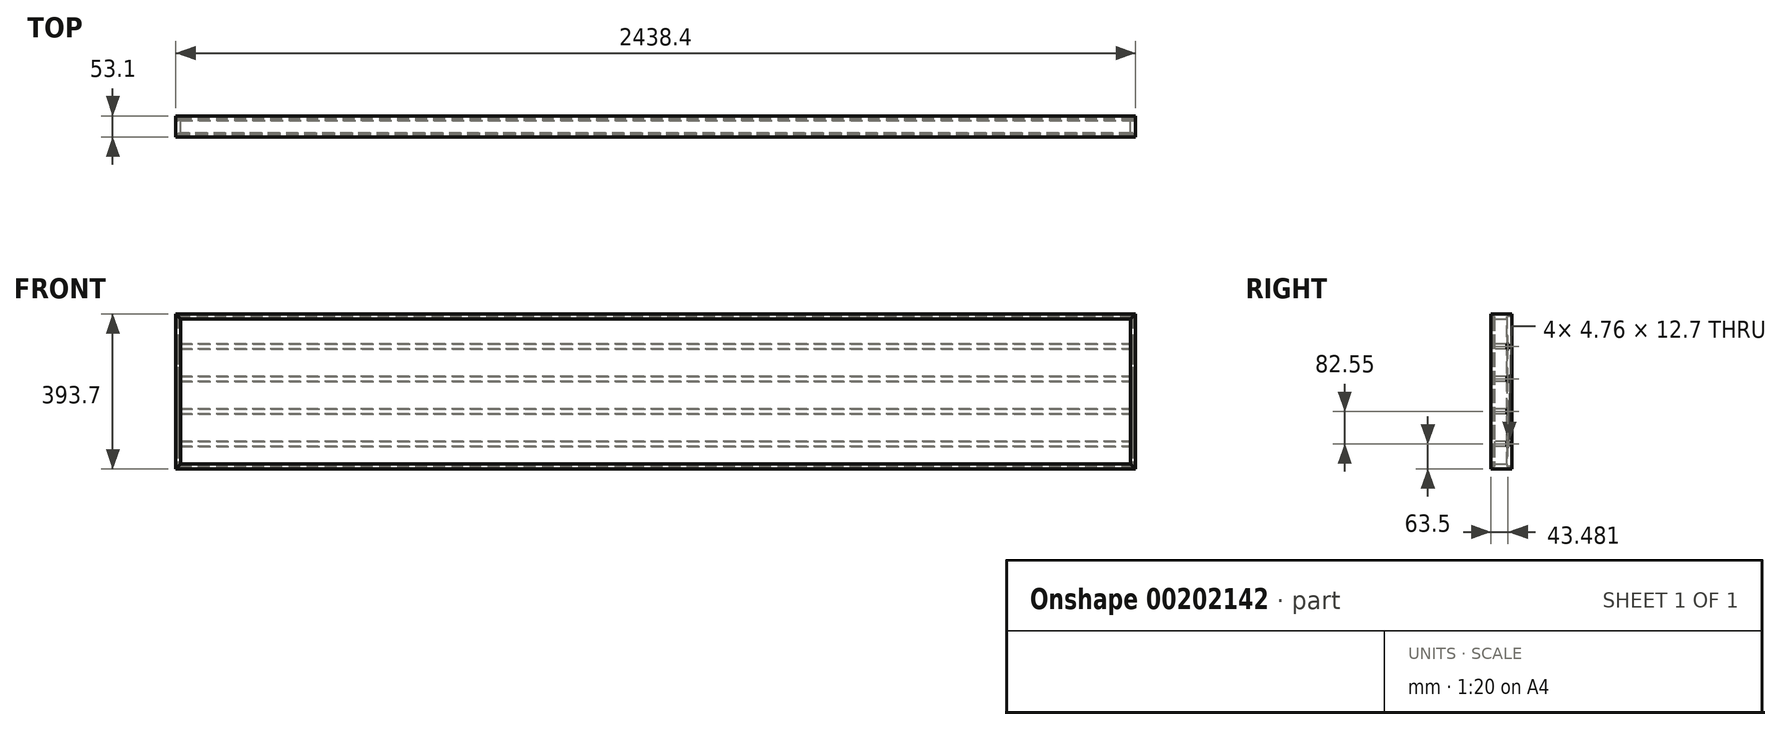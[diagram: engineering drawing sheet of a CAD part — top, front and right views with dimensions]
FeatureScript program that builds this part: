
annotation { "Feature Type Name" : "Feature", "Feature Type Description" : "" }
export const myFeature = defineFeature(function(context is Context, id is Id, definition is map)
    precondition{}
    {
        {
            var Q0;
            Q0=qCreatedBy(makeId("Right.planeOp"),FACE);
            var sketch = newSketch(context, id + "F0", { "sketchPlane" : qUnion([Q0])});
            skLineSegment(sketch, "E0.bottom", {"start": v(0, 0) * mm, "end": v(-12, 0) * mm});
            skLineSegment(sketch, "E0.top", {"start": v(0, -393.7) * mm, "end": v(-12, -393.7) * mm});
            skLineSegment(sketch, "E0.left", {"start": v(0, 0) * mm, "end": v(0, -393.7) * mm});
            skLineSegment(sketch, "E0.right", {"start": v(-12, 0) * mm, "end": v(-12, -393.7) * mm});
            skLineSegment(sketch, "E1.bottom", {"start": v(0, 0) * mm, "end": v(-53.1, 0) * mm});
            skLineSegment(sketch, "E1.top", {"start": v(0, -12.7) * mm, "end": v(-53.1, -12.7) * mm});
            skLineSegment(sketch, "E1.left", {"start": v(0, 0) * mm, "end": v(0, -12.7) * mm});
            skLineSegment(sketch, "E1.right", {"start": v(-53.1, 0) * mm, "end": v(-53.1, -12.7) * mm});
            skLineSegment(sketch, "E2.bottom", {"start": v(-7.24, -76.2) * mm, "end": v(-43.75, -76.2) * mm});
            skLineSegment(sketch, "E2.top", {"start": v(-7.24, -88.9) * mm, "end": v(-43.75, -88.9) * mm});
            skLineSegment(sketch, "E2.left", {"start": v(-7.24, -76.2) * mm, "end": v(-7.24, -88.9) * mm});
            skLineSegment(sketch, "E2.right", {"start": v(-43.75, -76.2) * mm, "end": v(-43.75, -88.9) * mm});
            skLineSegment(sketch, "E3.0.1.0", {"start": v(-7.24, -152.4) * mm, "end": v(-7.24, -165.1) * mm});
            skLineSegment(sketch, "E3.0.1.1", {"start": v(-7.24, -152.4) * mm, "end": v(-43.75, -152.4) * mm});
            skLineSegment(sketch, "E3.0.1.2", {"start": v(-43.75, -152.4) * mm, "end": v(-43.75, -165.1) * mm});
            skLineSegment(sketch, "E3.0.1.3", {"start": v(-7.24, -165.1) * mm, "end": v(-43.75, -165.1) * mm});
            skLineSegment(sketch, "E3.0.2.0", {"start": v(-7.24, -228.6) * mm, "end": v(-7.24, -241.3) * mm});
            skLineSegment(sketch, "E3.0.2.1", {"start": v(-7.24, -228.6) * mm, "end": v(-43.75, -228.6) * mm});
            skLineSegment(sketch, "E3.0.2.2", {"start": v(-43.75, -228.6) * mm, "end": v(-43.75, -241.3) * mm});
            skLineSegment(sketch, "E3.0.2.3", {"start": v(-7.24, -241.3) * mm, "end": v(-43.75, -241.3) * mm});
            skLineSegment(sketch, "E3.0.3.0", {"start": v(-7.24, -304.8) * mm, "end": v(-7.24, -317.5) * mm});
            skLineSegment(sketch, "E3.0.3.1", {"start": v(-7.24, -304.8) * mm, "end": v(-43.75, -304.8) * mm});
            skLineSegment(sketch, "E3.0.3.2", {"start": v(-43.75, -304.8) * mm, "end": v(-43.75, -317.5) * mm});
            skLineSegment(sketch, "E3.0.3.3", {"start": v(-7.24, -317.5) * mm, "end": v(-43.75, -317.5) * mm});
            skLineSegment(sketch, "E3.direction1", {"start": v(-43.75, -88.9) * mm, "end": v(-15.38, -88.9) * mm, "construction": true});
            skLineSegment(sketch, "E3.direction2", {"start": v(-43.75, -88.9) * mm, "end": v(-43.75, -165.1) * mm, "construction": true});
            skLineSegment(sketch, "E4.bottom", {"start": v(0, -393.7) * mm, "end": v(-53.1, -393.7) * mm});
            skLineSegment(sketch, "E4.top", {"start": v(0, -381) * mm, "end": v(-53.1, -381) * mm});
            skLineSegment(sketch, "E4.left", {"start": v(0, -393.7) * mm, "end": v(0, -381) * mm});
            skLineSegment(sketch, "E4.right", {"start": v(-53.1, -393.7) * mm, "end": v(-53.1, -381) * mm});
            skLineSegment(sketch, "E5", {"start": v(-25.5, -76.2) * mm, "end": v(-25.5, -12.7) * mm, "construction": true});
            skLineSegment(sketch, "E6", {"start": v(-25.5, -88.9) * mm, "end": v(-25.5, -152.4) * mm, "construction": true});
            skLineSegment(sketch, "E7", {"start": v(-25.5, -317.5) * mm, "end": v(-25.5, -381) * mm, "construction": true});
            skLineSegment(sketch, "E8.bottom", {"start": v(-43.75, -6.35) * mm, "end": v(-46.75, -6.35) * mm, "construction": true});
            skLineSegment(sketch, "E8.top", {"start": v(-43.75, -387.35) * mm, "end": v(-46.75, -387.35) * mm, "construction": true});
            skLineSegment(sketch, "E8.left", {"start": v(-43.75, -6.35) * mm, "end": v(-43.75, -387.35) * mm, "construction": true});
            skLineSegment(sketch, "E8.right", {"start": v(-46.75, -6.35) * mm, "end": v(-46.75, -387.35) * mm, "construction": true});
            skSolve(sketch);
        }
        {
            var Q0;
            Q0=qCreatedBy(makeId("Right.planeOp"),FACE);
            var sketch = newSketch(context, id + "F1", { "sketchPlane" : qUnion([Q0])});
            skLineSegment(sketch, "E9.0", {"start": v(-12, 0) * mm, "end": v(-12, -393.7) * mm, "construction": true});
            skLineSegment(sketch, "E10.0", {"start": v(0, 0) * mm, "end": v(-53.1, 0) * mm});
            skLineSegment(sketch, "E10.1", {"start": v(-53.1, 0) * mm, "end": v(-53.1, -12.7) * mm});
            skLineSegment(sketch, "E10.2", {"start": v(0, -12.7) * mm, "end": v(-53.1, -12.7) * mm});
            skLineSegment(sketch, "E10.3", {"start": v(0, 0) * mm, "end": v(0, -12.7) * mm});
            skSolve(sketch);
        }
        {
            var Q0;
            Q0 = qSketchRegion(id + "F1", true);
            extrude(context, id + "F2", {"entities" : qUnion([Q0]), "depth" : 1219.2 * mm, "hasSecondDirection" : true, "secondDirectionOppositeDirection" : true, "secondDirectionDepth" : 1219.2 * mm});
        }
        {
            var Q0;
            Q0=qCreatedBy(makeId("Right.planeOp"),FACE);
            var sketch = newSketch(context, id + "F3", { "sketchPlane" : qUnion([Q0])});
            skLineSegment(sketch, "E11.0", {"start": v(-12, 0) * mm, "end": v(-12, -393.7) * mm, "construction": true});
            skLineSegment(sketch, "E12.0", {"start": v(0, -393.7) * mm, "end": v(-53.1, -393.7) * mm});
            skLineSegment(sketch, "E12.1", {"start": v(-53.1, -393.7) * mm, "end": v(-53.1, -381) * mm});
            skLineSegment(sketch, "E12.2", {"start": v(0, -381) * mm, "end": v(-53.1, -381) * mm});
            skLineSegment(sketch, "E12.3", {"start": v(0, -393.7) * mm, "end": v(0, -381) * mm});
            skSolve(sketch);
        }
        {
            var Q0;
            Q0 = qSketchRegion(id + "F3", true);
            extrude(context, id + "F4", {"entities" : qUnion([Q0]), "depth" : 1219.2 * mm, "hasSecondDirection" : true, "secondDirectionOppositeDirection" : true, "secondDirectionDepth" : 1219.2 * mm});
        }
        {
            var Q0;
            Q0=qCreatedBy(makeId("Right.planeOp"),FACE);
            var sketch = newSketch(context, id + "F5", { "sketchPlane" : qUnion([Q0])});
            skPoint(sketch, "E13.orphan", {"position": v(-43.75, -76.2) * mm});
            skPoint(sketch, "E14.orphan", {"position": v(-43.75, -88.9) * mm});
            skPoint(sketch, "E15.orphan", {"position": v(-43.75, -152.4) * mm});
            skPoint(sketch, "E16.orphan", {"position": v(-43.75, -165.1) * mm});
            skPoint(sketch, "E17.orphan", {"position": v(-43.75, -228.6) * mm});
            skPoint(sketch, "E18.orphan", {"position": v(-43.75, -241.3) * mm});
            skPoint(sketch, "E19.orphan", {"position": v(-43.75, -304.8) * mm});
            skPoint(sketch, "E20.orphan", {"position": v(-43.75, -317.5) * mm});
            skLineSegment(sketch, "E21.bottom", {"start": v(0, -6.35) * mm, "end": v(-12, -6.35) * mm});
            skLineSegment(sketch, "E21.top", {"start": v(0, -387.35) * mm, "end": v(-12, -387.35) * mm});
            skLineSegment(sketch, "E21.left", {"start": v(0, -6.35) * mm, "end": v(0, -387.35) * mm});
            skLineSegment(sketch, "E21.right", {"start": v(-12, -6.35) * mm, "end": v(-12, -387.35) * mm});
            skSolve(sketch);
        }
        {
            var Q0;
            Q0 = qSketchRegion(id + "F5", true);
            extrude(context, id + "F6", {"entities" : qUnion([Q0]), "depth" : 1212.85 * mm, "hasSecondDirection" : true, "secondDirectionOppositeDirection" : true, "secondDirectionDepth" : 1212.85 * mm});
        }
        {
            var Q0;
            Q0=qCreatedBy(makeId("Front.planeOp"),FACE);
            var sketch = newSketch(context, id + "F7", { "sketchPlane" : qUnion([Q0])});
            skPoint(sketch, "E22.0", {"position": v(-1219.2, 0) * mm});
            skLineSegment(sketch, "E23.left", {"start": v(-1219.2, 0) * mm, "end": v(-1219.2, -393.7) * mm});
            skLineSegment(sketch, "E23.right", {"start": v(-1206.5, -12.7) * mm, "end": v(-1206.5, -381) * mm});
            skLineSegment(sketch, "E24", {"start": v(-1219.2, 0) * mm, "end": v(-1206.5, -12.7) * mm});
            skLineSegment(sketch, "E25", {"start": v(-1219.2, -393.7) * mm, "end": v(-1206.5, -381) * mm});
            skPoint(sketch, "E26.0", {"position": v(1219.2, 0) * mm});
            skPoint(sketch, "E26.1", {"position": v(1219.2, -393.7) * mm});
            skLineSegment(sketch, "E27.left", {"start": v(1219.2, 0) * mm, "end": v(1219.2, -393.7) * mm});
            skLineSegment(sketch, "E27.right", {"start": v(1206.5, -12.7) * mm, "end": v(1206.5, -381) * mm});
            skLineSegment(sketch, "E28", {"start": v(1219.2, 0) * mm, "end": v(1206.5, -12.7) * mm});
            skLineSegment(sketch, "E29", {"start": v(1219.2, -393.7) * mm, "end": v(1206.5, -381) * mm});
            skSolve(sketch);
        }
        {
            var Q0;
            Q0 = qSketchRegion(id + "F7", true);
            var Q1;
            Q1=makeQuery(id+"F2.opExtrude","SWEPT_FACE",FACE,{"disambiguationData":[OSD([sQuery(id+"F1.wireOp",EDGE,"E10.1")])]});
            extrude(context, id + "F8", {"entities" : qUnion([Q0]), "endBound" : BoundingType.UP_TO_SURFACE, "endBoundEntityFace" : qUnion([Q1]), "depth" : 63.5 * mm});
        }
        {
            var Q0;
            Q0=qCreatedBy(makeId("Right.planeOp"),FACE);
            var sketch = newSketch(context, id + "F9", { "sketchPlane" : qUnion([Q0])});
            skLineSegment(sketch, "E30.0", {"start": v(-7.24, -76.2) * mm, "end": v(-43.75, -76.2) * mm});
            skLineSegment(sketch, "E30.1", {"start": v(-43.75, -76.2) * mm, "end": v(-43.75, -88.9) * mm});
            skLineSegment(sketch, "E30.2", {"start": v(-7.24, -88.9) * mm, "end": v(-43.75, -88.9) * mm});
            skLineSegment(sketch, "E30.3", {"start": v(-7.24, -76.2) * mm, "end": v(-7.24, -88.9) * mm});
            skSolve(sketch);
        }
        {
            var Q0;
            Q0 = qSketchRegion(id + "F9", true);
            var Q1;
            Q1=makeQuery(id+"F8.opExtrude","SWEPT_FACE",FACE,{"disambiguationData":[OSD([sQuery(id+"F7.wireOp",EDGE,"E27.right")])]});
            var Q2;
            Q2=makeQuery(id+"F8.opExtrude","SWEPT_FACE",FACE,{"disambiguationData":[OSD([sQuery(id+"F7.wireOp",EDGE,"E23.right")])]});
            extrude(context, id + "F10", {"entities" : qUnion([Q0]), "endBound" : BoundingType.UP_TO_SURFACE, "endBoundEntityFace" : qUnion([Q1]), "depth" : 1206.5 * mm, "hasSecondDirection" : true, "secondDirectionBound" : BoundingType.UP_TO_SURFACE, "secondDirectionOppositeDirection" : true, "secondDirectionBoundEntityFace" : qUnion([Q2]), "secondDirectionDepth" : 1206.5 * mm});
        }
        {
            var Q0;
            Q0=makeQuery(id+"F10.opExtrude","SWEPT_BODY",BODY,{"disambiguationData":[OSD([sQuery(id+"F9.wireOp",EDGE,"E30.0"),sQuery(id+"F9.wireOp",EDGE,"E30.1"),sQuery(id+"F9.wireOp",EDGE,"E30.2"),sQuery(id+"F9.wireOp",EDGE,"E30.3")])]});
            transform(context, id + "F11", {"entities" : qUnion([Q0]), "transformType" : TransformType.TRANSLATION_3D, "dx" : 0 * mm, "dy" : 0 * mm, "dz" : -82.55 * mm, "makeCopy" : true});
        }
        {
            var Q0;
            Q0=makeQuery(id+"F11.opPattern","COPY",BODY,{"derivedFrom":makeQuery(id+"F10.opExtrude","SWEPT_BODY",BODY,{"disambiguationData":[OSD([sQuery(id+"F9.wireOp",EDGE,"E30.0"),sQuery(id+"F9.wireOp",EDGE,"E30.1"),sQuery(id+"F9.wireOp",EDGE,"E30.2"),sQuery(id+"F9.wireOp",EDGE,"E30.3")])]}),"instanceName":"1"});
            transform(context, id + "F12", {"entities" : qUnion([Q0]), "transformType" : TransformType.TRANSLATION_3D, "dx" : 0 * mm, "dy" : 0 * mm, "dz" : -82.55 * mm, "makeCopy" : true});
        }
        {
            var Q0;
            Q0=makeQuery(id+"F12.opPattern","COPY",BODY,{"derivedFrom":makeQuery(id+"F11.opPattern","COPY",BODY,{"derivedFrom":makeQuery(id+"F10.opExtrude","SWEPT_BODY",BODY,{"disambiguationData":[OSD([sQuery(id+"F9.wireOp",EDGE,"E30.0"),sQuery(id+"F9.wireOp",EDGE,"E30.1"),sQuery(id+"F9.wireOp",EDGE,"E30.2"),sQuery(id+"F9.wireOp",EDGE,"E30.3")])]}),"instanceName":"1"}),"instanceName":"1"});
            transform(context, id + "F13", {"entities" : qUnion([Q0]), "transformType" : TransformType.TRANSLATION_3D, "dx" : 0 * mm, "dy" : 0 * mm, "dz" : -82.55 * mm, "makeCopy" : true});
        }
        {
            var Q0;
            Q0=makeQuery(id+"F8.opExtrude","SWEPT_BODY",BODY,{"disambiguationData":[OSD([sQuery(id+"F7.wireOp",EDGE,"E23.left"),sQuery(id+"F7.wireOp",EDGE,"E23.right"),sQuery(id+"F7.wireOp",EDGE,"E24"),sQuery(id+"F7.wireOp",EDGE,"E25")])]});
            var Q1;
            Q1=makeQuery(id+"F8.opExtrude","SWEPT_BODY",BODY,{"disambiguationData":[OSD([sQuery(id+"F7.wireOp",EDGE,"E27.left"),sQuery(id+"F7.wireOp",EDGE,"E27.right"),sQuery(id+"F7.wireOp",EDGE,"E28"),sQuery(id+"F7.wireOp",EDGE,"E29")])]});
            var Q2;
            Q2=makeQuery(id+"F2.opExtrude","SWEPT_BODY",BODY,{"disambiguationData":[OSD([sQuery(id+"F1.wireOp",EDGE,"E10.0"),sQuery(id+"F1.wireOp",EDGE,"E10.1"),sQuery(id+"F1.wireOp",EDGE,"E10.2"),sQuery(id+"F1.wireOp",EDGE,"E10.3")])]});
            var Q3;
            Q3=makeQuery(id+"F4.opExtrude","SWEPT_BODY",BODY,{"disambiguationData":[OSD([sQuery(id+"F3.wireOp",EDGE,"E12.0"),sQuery(id+"F3.wireOp",EDGE,"E12.1"),sQuery(id+"F3.wireOp",EDGE,"E12.2"),sQuery(id+"F3.wireOp",EDGE,"E12.3")])]});
            booleanBodies(context, id + "F14", {"operationType" : BooleanOperationType.SUBTRACTION, "tools" : qUnion([Q0, Q1]), "targets" : qUnion([Q2, Q3]), "keepTools" : true});
        }
        {
            var Q0;
            Q0=makeQuery(id+"F6.opExtrude","SWEPT_BODY",BODY,{"disambiguationData":[OSD([sQuery(id+"F5.wireOp",EDGE,"E21.bottom"),sQuery(id+"F5.wireOp",EDGE,"E21.top"),sQuery(id+"F5.wireOp",EDGE,"E21.left"),sQuery(id+"F5.wireOp",EDGE,"E21.right")])]});
            var Q1;
            Q1=makeQuery(id+"F8.opExtrude","SWEPT_BODY",BODY,{"disambiguationData":[OSD([sQuery(id+"F7.wireOp",EDGE,"E23.left"),sQuery(id+"F7.wireOp",EDGE,"E23.right"),sQuery(id+"F7.wireOp",EDGE,"E24"),sQuery(id+"F7.wireOp",EDGE,"E25")])]});
            var Q2;
            Q2=makeQuery(id+"F8.opExtrude","SWEPT_BODY",BODY,{"disambiguationData":[OSD([sQuery(id+"F7.wireOp",EDGE,"E27.left"),sQuery(id+"F7.wireOp",EDGE,"E27.right"),sQuery(id+"F7.wireOp",EDGE,"E28"),sQuery(id+"F7.wireOp",EDGE,"E29")])]});
            var Q3;
            Q3=makeQuery(id+"F2.opExtrude","SWEPT_BODY",BODY,{"disambiguationData":[OSD([sQuery(id+"F1.wireOp",EDGE,"E10.0"),sQuery(id+"F1.wireOp",EDGE,"E10.1"),sQuery(id+"F1.wireOp",EDGE,"E10.2"),sQuery(id+"F1.wireOp",EDGE,"E10.3")])]});
            var Q4;
            Q4=makeQuery(id+"F4.opExtrude","SWEPT_BODY",BODY,{"disambiguationData":[OSD([sQuery(id+"F3.wireOp",EDGE,"E12.0"),sQuery(id+"F3.wireOp",EDGE,"E12.1"),sQuery(id+"F3.wireOp",EDGE,"E12.2"),sQuery(id+"F3.wireOp",EDGE,"E12.3")])]});
            booleanBodies(context, id + "F15", {"operationType" : BooleanOperationType.SUBTRACTION, "tools" : qUnion([Q0]), "targets" : qUnion([Q1, Q2, Q3, Q4]), "keepTools" : true});
        }
        {
            var Q0;
            Q0=makeQuery(id+"F10.opExtrude","SWEPT_BODY",BODY,{"disambiguationData":[OSD([sQuery(id+"F9.wireOp",EDGE,"E30.0"),sQuery(id+"F9.wireOp",EDGE,"E30.1"),sQuery(id+"F9.wireOp",EDGE,"E30.2"),sQuery(id+"F9.wireOp",EDGE,"E30.3")])]});
            var Q1;
            Q1=makeQuery(id+"F11.opPattern","COPY",BODY,{"derivedFrom":makeQuery(id+"F10.opExtrude","SWEPT_BODY",BODY,{"disambiguationData":[OSD([sQuery(id+"F9.wireOp",EDGE,"E30.0"),sQuery(id+"F9.wireOp",EDGE,"E30.1"),sQuery(id+"F9.wireOp",EDGE,"E30.2"),sQuery(id+"F9.wireOp",EDGE,"E30.3")])]}),"instanceName":"1"});
            var Q2;
            Q2=makeQuery(id+"F12.opPattern","COPY",BODY,{"derivedFrom":makeQuery(id+"F11.opPattern","COPY",BODY,{"derivedFrom":makeQuery(id+"F10.opExtrude","SWEPT_BODY",BODY,{"disambiguationData":[OSD([sQuery(id+"F9.wireOp",EDGE,"E30.0"),sQuery(id+"F9.wireOp",EDGE,"E30.1"),sQuery(id+"F9.wireOp",EDGE,"E30.2"),sQuery(id+"F9.wireOp",EDGE,"E30.3")])]}),"instanceName":"1"}),"instanceName":"1"});
            var Q3;
            Q3=makeQuery(id+"F13.opPattern","COPY",BODY,{"derivedFrom":makeQuery(id+"F12.opPattern","COPY",BODY,{"derivedFrom":makeQuery(id+"F11.opPattern","COPY",BODY,{"derivedFrom":makeQuery(id+"F10.opExtrude","SWEPT_BODY",BODY,{"disambiguationData":[OSD([sQuery(id+"F9.wireOp",EDGE,"E30.0"),sQuery(id+"F9.wireOp",EDGE,"E30.1"),sQuery(id+"F9.wireOp",EDGE,"E30.2"),sQuery(id+"F9.wireOp",EDGE,"E30.3")])]}),"instanceName":"1"}),"instanceName":"1"}),"instanceName":"1"});
            var Q4;
            Q4=makeQuery(id+"F6.opExtrude","SWEPT_BODY",BODY,{"disambiguationData":[OSD([sQuery(id+"F5.wireOp",EDGE,"E21.bottom"),sQuery(id+"F5.wireOp",EDGE,"E21.top"),sQuery(id+"F5.wireOp",EDGE,"E21.left"),sQuery(id+"F5.wireOp",EDGE,"E21.right")])]});
            booleanBodies(context, id + "F16", {"operationType" : BooleanOperationType.SUBTRACTION, "tools" : qUnion([Q0, Q1, Q2, Q3]), "targets" : qUnion([Q4]), "keepTools" : true});
        }
        {
            var Q0;
            Q0=qCreatedBy(makeId("Right.planeOp"),FACE);
            var sketch = newSketch(context, id + "F17", { "sketchPlane" : qUnion([Q0])});
            skLineSegment(sketch, "E31.0.0", {"start": v(-12, -158.75) * mm, "end": v(-12, -171.45) * mm});
            skLineSegment(sketch, "E31.0.1", {"start": v(-12, -171.45) * mm, "end": v(-7.24, -171.45) * mm});
            skLineSegment(sketch, "E31.0.2", {"start": v(-7.24, -171.45) * mm, "end": v(-7.24, -158.75) * mm});
            skLineSegment(sketch, "E31.0.3", {"start": v(-7.24, -158.75) * mm, "end": v(-12, -158.75) * mm});
            skLineSegment(sketch, "E31.1.0", {"start": v(-12, -76.2) * mm, "end": v(-12, -88.9) * mm});
            skLineSegment(sketch, "E31.1.1", {"start": v(-12, -88.9) * mm, "end": v(-7.24, -88.9) * mm});
            skLineSegment(sketch, "E31.1.2", {"start": v(-7.24, -88.9) * mm, "end": v(-7.24, -76.2) * mm});
            skLineSegment(sketch, "E31.1.3", {"start": v(-7.24, -76.2) * mm, "end": v(-12, -76.2) * mm});
            skLineSegment(sketch, "E31.2.0", {"start": v(-12, -241.3) * mm, "end": v(-12, -254) * mm});
            skLineSegment(sketch, "E31.2.1", {"start": v(-12, -254) * mm, "end": v(-7.24, -254) * mm});
            skLineSegment(sketch, "E31.2.2", {"start": v(-7.24, -254) * mm, "end": v(-7.24, -241.3) * mm});
            skLineSegment(sketch, "E31.2.3", {"start": v(-7.24, -241.3) * mm, "end": v(-12, -241.3) * mm});
            skLineSegment(sketch, "E31.3.0", {"start": v(-12, -323.85) * mm, "end": v(-12, -336.55) * mm});
            skLineSegment(sketch, "E31.3.1", {"start": v(-12, -336.55) * mm, "end": v(-7.24, -336.55) * mm});
            skLineSegment(sketch, "E31.3.2", {"start": v(-7.24, -336.55) * mm, "end": v(-7.24, -323.85) * mm});
            skLineSegment(sketch, "E31.3.3", {"start": v(-7.24, -323.85) * mm, "end": v(-12, -323.85) * mm});
            skSolve(sketch);
        }
        {
            var Q0;
            Q0 = qSketchRegion(id + "F17", true);
            extrude(context, id + "F18", {"entities" : qUnion([Q0]), "operationType" : NewBodyOperationType.REMOVE, "endBound" : BoundingType.THROUGH_ALL, "oppositeDirection" : true, "depth" : 25.4 * mm, "hasSecondDirection" : true, "secondDirectionBound" : BoundingType.THROUGH_ALL, "secondDirectionOppositeDirection" : false, "secondDirectionDepth" : 25.4 * mm});
        }
        {
            var Q0;
            Q0=makeQuery(id+"F10.opExtrude","SWEPT_FACE",FACE,{"disambiguationData":[OSD([sQuery(id+"F9.wireOp",EDGE,"E30.1")])]});
            var sketch = newSketch(context, id + "F19", { "sketchPlane" : qUnion([Q0])});
            skLineSegment(sketch, "E32.bottom", {"start": v(-1212.85, -6.35) * mm, "end": v(1212.85, -6.35) * mm});
            skLineSegment(sketch, "E32.top", {"start": v(-1212.85, -387.35) * mm, "end": v(1212.85, -387.35) * mm});
            skLineSegment(sketch, "E32.left", {"start": v(-1212.85, -6.35) * mm, "end": v(-1212.85, -387.35) * mm});
            skLineSegment(sketch, "E32.right", {"start": v(1212.85, -6.35) * mm, "end": v(1212.85, -387.35) * mm});
            skSolve(sketch);
        }
        {
            var Q0;
            Q0 = qSketchRegion(id + "F19", true);
            extrude(context, id + "F20", {"entities" : qUnion([Q0]), "depth" : 3.17 * mm});
        }
        {
            var Q0;
            Q0=makeQuery(id+"F20.opExtrude","SWEPT_BODY",BODY,{"disambiguationData":[OSD([sQuery(id+"F19.wireOp",EDGE,"E32.bottom"),sQuery(id+"F19.wireOp",EDGE,"E32.top"),sQuery(id+"F19.wireOp",EDGE,"E32.left"),sQuery(id+"F19.wireOp",EDGE,"E32.right")])]});
            transform(context, id + "F21", {"entities" : qUnion([Q0]), "transformType" : TransformType.TRANSLATION_3D, "dx" : 0 * mm, "dy" : -1.59 * mm, "dz" : 0 * mm, "makeCopy" : true});
        }
        {
            var Q0;
            Q0=makeQuery(id+"F20.opExtrude","SWEPT_BODY",BODY,{"disambiguationData":[OSD([sQuery(id+"F19.wireOp",EDGE,"E32.bottom"),sQuery(id+"F19.wireOp",EDGE,"E32.top"),sQuery(id+"F19.wireOp",EDGE,"E32.left"),sQuery(id+"F19.wireOp",EDGE,"E32.right")])]});
            var Q1;
            Q1=makeQuery(id+"F8.opExtrude","SWEPT_BODY",BODY,{"disambiguationData":[OSD([sQuery(id+"F7.wireOp",EDGE,"E23.left"),sQuery(id+"F7.wireOp",EDGE,"E23.right"),sQuery(id+"F7.wireOp",EDGE,"E24"),sQuery(id+"F7.wireOp",EDGE,"E25")])]});
            var Q2;
            Q2=makeQuery(id+"F8.opExtrude","SWEPT_BODY",BODY,{"disambiguationData":[OSD([sQuery(id+"F7.wireOp",EDGE,"E27.left"),sQuery(id+"F7.wireOp",EDGE,"E27.right"),sQuery(id+"F7.wireOp",EDGE,"E28"),sQuery(id+"F7.wireOp",EDGE,"E29")])]});
            var Q3;
            Q3=makeQuery(id+"F2.opExtrude","SWEPT_BODY",BODY,{"disambiguationData":[OSD([sQuery(id+"F1.wireOp",EDGE,"E10.0"),sQuery(id+"F1.wireOp",EDGE,"E10.1"),sQuery(id+"F1.wireOp",EDGE,"E10.2"),sQuery(id+"F1.wireOp",EDGE,"E10.3")])]});
            var Q4;
            Q4=makeQuery(id+"F4.opExtrude","SWEPT_BODY",BODY,{"disambiguationData":[OSD([sQuery(id+"F3.wireOp",EDGE,"E12.0"),sQuery(id+"F3.wireOp",EDGE,"E12.1"),sQuery(id+"F3.wireOp",EDGE,"E12.2"),sQuery(id+"F3.wireOp",EDGE,"E12.3")])]});
            booleanBodies(context, id + "F22", {"operationType" : BooleanOperationType.SUBTRACTION, "tools" : qUnion([Q0]), "targets" : qUnion([Q1, Q2, Q3, Q4]), "keepTools" : true});
        }
        {
            var Q0;
            Q0=makeQuery(id+"F21.opPattern","COPY",BODY,{"derivedFrom":makeQuery(id+"F20.opExtrude","SWEPT_BODY",BODY,{"disambiguationData":[OSD([sQuery(id+"F19.wireOp",EDGE,"E32.bottom"),sQuery(id+"F19.wireOp",EDGE,"E32.top"),sQuery(id+"F19.wireOp",EDGE,"E32.left"),sQuery(id+"F19.wireOp",EDGE,"E32.right")])]}),"instanceName":"1"});
            var Q1;
            Q1=makeQuery(id+"F8.opExtrude","SWEPT_BODY",BODY,{"disambiguationData":[OSD([sQuery(id+"F7.wireOp",EDGE,"E27.left"),sQuery(id+"F7.wireOp",EDGE,"E27.right"),sQuery(id+"F7.wireOp",EDGE,"E28"),sQuery(id+"F7.wireOp",EDGE,"E29")])]});
            var Q2;
            Q2=makeQuery(id+"F8.opExtrude","SWEPT_BODY",BODY,{"disambiguationData":[OSD([sQuery(id+"F7.wireOp",EDGE,"E23.left"),sQuery(id+"F7.wireOp",EDGE,"E23.right"),sQuery(id+"F7.wireOp",EDGE,"E24"),sQuery(id+"F7.wireOp",EDGE,"E25")])]});
            var Q3;
            Q3=makeQuery(id+"F4.opExtrude","SWEPT_BODY",BODY,{"disambiguationData":[OSD([sQuery(id+"F3.wireOp",EDGE,"E12.0"),sQuery(id+"F3.wireOp",EDGE,"E12.1"),sQuery(id+"F3.wireOp",EDGE,"E12.2"),sQuery(id+"F3.wireOp",EDGE,"E12.3")])]});
            var Q4;
            Q4=makeQuery(id+"F2.opExtrude","SWEPT_BODY",BODY,{"disambiguationData":[OSD([sQuery(id+"F1.wireOp",EDGE,"E10.0"),sQuery(id+"F1.wireOp",EDGE,"E10.1"),sQuery(id+"F1.wireOp",EDGE,"E10.2"),sQuery(id+"F1.wireOp",EDGE,"E10.3")])]});
            booleanBodies(context, id + "F23", {"operationType" : BooleanOperationType.SUBTRACTION, "tools" : qUnion([Q0]), "targets" : qUnion([Q1, Q2, Q3, Q4])});
        }
    });
